# Revit family: Shower_Slide_Bar-GROHE-Tempesta-26922_Series
name_source: partatom
category: Plumbing Fixtures
units: mm (PartAtom-declared; Revit-internal decimal feet)

## family parameters
Cut with Voids When Loaded = No
Host = Face
OmniClass Number = 23.45.05.14.17
OmniClass Title = Showers
Part Type = Normal
Room Calculation Point = No
Round Connector Dimension = Use Diameter
Shared = Yes

## types (3) — shared parameters
Adjustable Height = 18 1/2"
Adjustable Height Constraint = 18 1/2"
Adjustable Height Constraint /2 = 9 1/4"
Assembly Code = D2010710
CEC Compliant = Yes
CW Connection = No
CWFU = 3
CalGreen Compliant = Yes
Compliance Certifications = • WaterSense• CEC Certified• CALGreen Compliant• Massachusetts Plumbing Board Approved• Energy Policy Act of 1992• CSA B125.1• ASME A112.18.1
Default Elevation = 0"
Description = 24” (900MM) SHOWER SLIDE BAR
HW Connection = No
HWFU = 3
Height = 18 1/2"
Holder Height from Base = 10"
Holder Height from Base Constraint = 8"
Installation Type = Wall Mounted
Manufacturer = Grohe
Tempered Connection Diameter = 1/2"
Type Comments = Adjustable hand shower holder glider
URL = https://www.grohe.com
Vent Connection = No
WFU = 4
Waste Connection = No
Width = 2 3/8"

## per-type parameters (varying)
| type | Finish | Material |
| 26922001 | Metal-Grohe-001-StarLight Chrome | Metal-Grohe-001-StarLight Chrome |
| 269222431 | Metal-Grohe-2431-Matte Black | Metal-Grohe-2431-Matte Black |
| 26922EN1 | Metal-Grohe-EN1-Brushed Nickel Infinity Finish | Metal-Grohe-EN1-Brushed Nickel Infinity Finish |

note: column(s) folded — value = type name in every type: Model

## geometry (parser evidence)
native form markers: Sweep x6
no freeform markers — native parametric forms only
